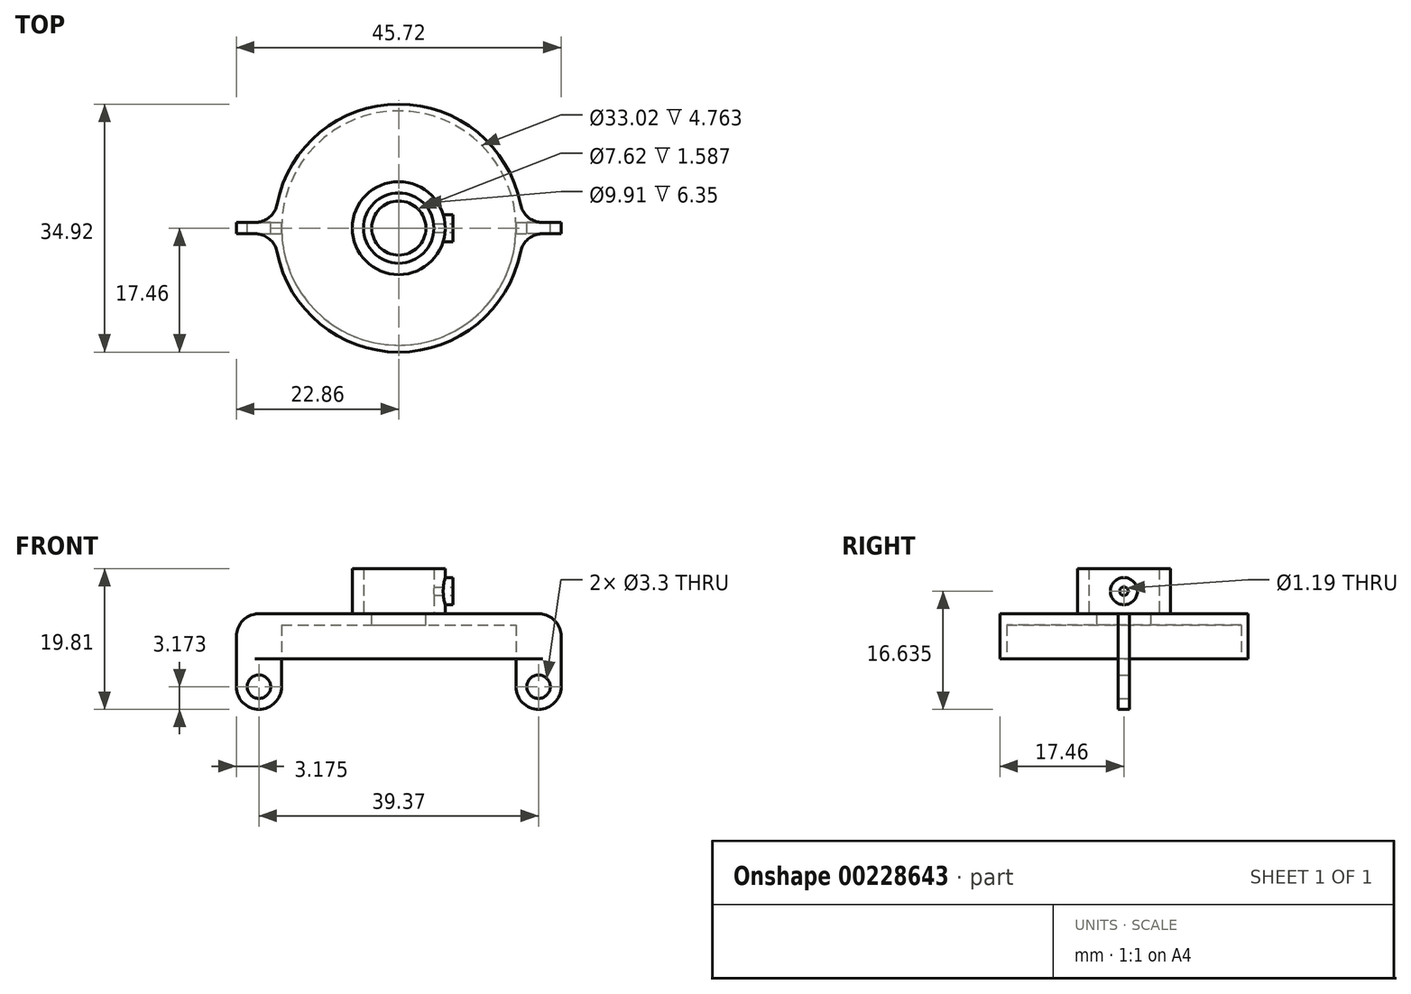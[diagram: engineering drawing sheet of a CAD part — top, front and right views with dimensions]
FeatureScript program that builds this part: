
annotation { "Feature Type Name" : "Feature", "Feature Type Description" : "" }
export const myFeature = defineFeature(function(context is Context, id is Id, definition is map)
    precondition{}
    {
        {
            var Q0;
            Q0=qCreatedBy(makeId("Top.planeOp"),FACE);
            var sketch = newSketch(context, id + "F0", { "sketchPlane" : qUnion([Q0])});
            skCircle(sketch, "E0", {"center": v(0, 0) * mm, "radius": 17.46 * mm});
            skSolve(sketch);
        }
        {
            var Q0;
            Q0 = qSketchRegion(id + "F0", true);
            extrude(context, id + "F1", {"entities" : qUnion([Q0]), "depth" : 6.35 * mm});
        }
        {
            var Q0;
            Q0=makeQuery(id+"F1.opExtrude","CAP_FACE",FACE,{"disambiguationData":[OSD([sQuery(id+"F0.wireOp",EDGE,"E0")])],"isStart":true});
            var sketch = newSketch(context, id + "F2", { "sketchPlane" : qUnion([Q0])});
            skCircle(sketch, "E1", {"center": v(0, 0) * mm, "radius": 16.51 * mm});
            skSolve(sketch);
        }
        {
            var Q0;
            Q0 = qSketchRegion(id + "F2", true);
            extrude(context, id + "F3", {"entities" : qUnion([Q0]), "operationType" : NewBodyOperationType.REMOVE, "oppositeDirection" : true, "depth" : 4.76 * mm});
        }
        {
            var Q0;
            Q0=makeQuery(id+"F1.opExtrude","CAP_FACE",FACE,{"disambiguationData":[OSD([sQuery(id+"F0.wireOp",EDGE,"E0")])],"isStart":false});
            var sketch = newSketch(context, id + "F4", { "sketchPlane" : qUnion([Q0])});
            skCircle(sketch, "E2", {"center": v(0, 0) * mm, "radius": 3.8 * mm});
            skSolve(sketch);
        }
        {
            var Q0;
            Q0 = qSketchRegion(id + "F4", true);
            extrude(context, id + "F5", {"entities" : qUnion([Q0]), "operationType" : NewBodyOperationType.REMOVE, "endBound" : BoundingType.THROUGH_ALL, "oppositeDirection" : true, "depth" : 25.4 * mm});
        }
        {
            var Q0;
            Q0=qCreatedBy(makeId("Front.planeOp"),FACE);
            var sketch = newSketch(context, id + "F6", { "sketchPlane" : qUnion([Q0])});
            skLineSegment(sketch, "E3.bottom", {"start": v(-16.51, 6.35) * mm, "end": v(-22.86, 6.35) * mm});
            skLineSegment(sketch, "E3.top", {"start": v(-16.51, -7.11) * mm, "end": v(-22.86, -7.11) * mm});
            skLineSegment(sketch, "E3.left", {"start": v(-16.51, 6.35) * mm, "end": v(-16.51, -7.11) * mm});
            skLineSegment(sketch, "E3.right", {"start": v(-22.86, 6.35) * mm, "end": v(-22.86, -7.11) * mm});
            skSolve(sketch);
        }
        {
            var Q0;
            Q0 = qSketchRegion(id + "F6", true);
            extrude(context, id + "F7", {"entities" : qUnion([Q0]), "endBound" : BoundingType.SYMMETRIC, "depth" : 1.59 * mm});
        }
        {
            var Q0;
            Q0=makeQuery(id+"F7.opExtrude","SWEPT_BODY",BODY,{"disambiguationData":[OSD([sQuery(id+"F6.wireOp",EDGE,"E3.bottom"),sQuery(id+"F6.wireOp",EDGE,"E3.top"),sQuery(id+"F6.wireOp",EDGE,"E3.left"),sQuery(id+"F6.wireOp",EDGE,"E3.right")])]});
            var Q1;
            Q1=qCreatedBy(makeId("Right.planeOp"),FACE);
            mirror(context, id + "F8", {"operationType" : NewBodyOperationType.ADD, "entities" : qUnion([Q0]), "mirrorPlane" : qUnion([Q1])});
        }
        {
            var Q0;
            Q0=makeQuery(id+"F7.opExtrude","SWEPT_EDGE",EDGE,{"disambiguationData":[OSD([sQuery(id+"F6.wireOp",EDGE,"E3.bottom"),sQuery(id+"F6.wireOp",EDGE,"E3.right")])]});
            var Q1;
            Q1=makeQuery(id+"F7.opExtrude","SWEPT_EDGE",EDGE,{"disambiguationData":[OSD([sQuery(id+"F6.wireOp",EDGE,"E3.top"),sQuery(id+"F6.wireOp",EDGE,"E3.right")])]});
            var Q2;
            Q2=makeQuery(id+"F7.opExtrude","SWEPT_EDGE",EDGE,{"disambiguationData":[OSD([sQuery(id+"F6.wireOp",EDGE,"E3.top"),sQuery(id+"F6.wireOp",EDGE,"E3.left")])]});
            var Q3;
            Q3=makeQuery(id+"F8.opPattern","COPY",EDGE,{"derivedFrom":makeQuery(id+"F7.opExtrude","SWEPT_EDGE",EDGE,{"disambiguationData":[OSD([sQuery(id+"F6.wireOp",EDGE,"E3.bottom"),sQuery(id+"F6.wireOp",EDGE,"E3.right")])]}),"instanceName":"1"});
            var Q4;
            Q4=makeQuery(id+"F8.opPattern","COPY",EDGE,{"derivedFrom":makeQuery(id+"F7.opExtrude","SWEPT_EDGE",EDGE,{"disambiguationData":[OSD([sQuery(id+"F6.wireOp",EDGE,"E3.top"),sQuery(id+"F6.wireOp",EDGE,"E3.right")])]}),"instanceName":"1"});
            var Q5;
            Q5=makeQuery(id+"F8.opPattern","COPY",EDGE,{"derivedFrom":makeQuery(id+"F7.opExtrude","SWEPT_EDGE",EDGE,{"disambiguationData":[OSD([sQuery(id+"F6.wireOp",EDGE,"E3.top"),sQuery(id+"F6.wireOp",EDGE,"E3.left")])]}),"instanceName":"1"});
            fillet(context, id + "F9", {"entities" : qUnion([Q0, Q1, Q2, Q3, Q4, Q5]), "radius" : 3.17 * mm, "tangentPropagation" : true, "allowEdgeOverflow" : false});
        }
        {
            var Q0;
            Q0=makeQuery(id+"F8.boolean.opBoolean","INTERSECT",EDGE,{"derivedFrom":[makeQuery(id+"F1.opExtrude","SWEPT_FACE",FACE,{"disambiguationData":[OSD([sQuery(id+"F0.wireOp",EDGE,"E0")])]}),makeQuery(id+"F7.opExtrude","CAP_FACE",FACE,{"disambiguationData":[OSD([sQuery(id+"F6.wireOp",EDGE,"E3.bottom"),sQuery(id+"F6.wireOp",EDGE,"E3.top"),sQuery(id+"F6.wireOp",EDGE,"E3.left"),sQuery(id+"F6.wireOp",EDGE,"E3.right")])],"isStart":false})]});
            var Q1;
            Q1=makeQuery(id+"F8.boolean.opBoolean","INTERSECT",EDGE,{"derivedFrom":[makeQuery(id+"F1.opExtrude","SWEPT_FACE",FACE,{"disambiguationData":[OSD([sQuery(id+"F0.wireOp",EDGE,"E0")])]}),makeQuery(id+"F7.opExtrude","CAP_FACE",FACE,{"disambiguationData":[OSD([sQuery(id+"F6.wireOp",EDGE,"E3.bottom"),sQuery(id+"F6.wireOp",EDGE,"E3.top"),sQuery(id+"F6.wireOp",EDGE,"E3.left"),sQuery(id+"F6.wireOp",EDGE,"E3.right")])],"isStart":true})]});
            var Q2;
            Q2=makeQuery(id+"F8.boolean.opBoolean","INTERSECT",EDGE,{"derivedFrom":[makeQuery(id+"F1.opExtrude","SWEPT_FACE",FACE,{"disambiguationData":[OSD([sQuery(id+"F0.wireOp",EDGE,"E0")])]}),makeQuery(id+"F8.opPattern","COPY",FACE,{"derivedFrom":makeQuery(id+"F7.opExtrude","CAP_FACE",FACE,{"disambiguationData":[OSD([sQuery(id+"F6.wireOp",EDGE,"E3.bottom"),sQuery(id+"F6.wireOp",EDGE,"E3.top"),sQuery(id+"F6.wireOp",EDGE,"E3.left"),sQuery(id+"F6.wireOp",EDGE,"E3.right")])],"isStart":false}),"instanceName":"1"})]});
            var Q3;
            Q3=makeQuery(id+"F8.boolean.opBoolean","INTERSECT",EDGE,{"derivedFrom":[makeQuery(id+"F1.opExtrude","SWEPT_FACE",FACE,{"disambiguationData":[OSD([sQuery(id+"F0.wireOp",EDGE,"E0")])]}),makeQuery(id+"F8.opPattern","COPY",FACE,{"derivedFrom":makeQuery(id+"F7.opExtrude","CAP_FACE",FACE,{"disambiguationData":[OSD([sQuery(id+"F6.wireOp",EDGE,"E3.bottom"),sQuery(id+"F6.wireOp",EDGE,"E3.top"),sQuery(id+"F6.wireOp",EDGE,"E3.left"),sQuery(id+"F6.wireOp",EDGE,"E3.right")])],"isStart":true}),"instanceName":"1"})]});
            fillet(context, id + "F10", {"entities" : qUnion([Q0, Q1, Q2, Q3]), "radius" : 3.17 * mm, "tangentPropagation" : true, "allowEdgeOverflow" : false});
        }
        {
            var Q0;
            Q0=makeQuery(id+"F7.opExtrude","CAP_FACE",FACE,{"disambiguationData":[OSD([sQuery(id+"F6.wireOp",EDGE,"E3.bottom"),sQuery(id+"F6.wireOp",EDGE,"E3.top"),sQuery(id+"F6.wireOp",EDGE,"E3.left"),sQuery(id+"F6.wireOp",EDGE,"E3.right")])],"isStart":true});
            var sketch = newSketch(context, id + "F11", { "sketchPlane" : qUnion([Q0])});
            skCircle(sketch, "E4", {"center": v(19.69, -3.94) * mm, "radius": 1.65 * mm});
            skCircle(sketch, "E5", {"center": v(-19.69, -3.94) * mm, "radius": 1.65 * mm});
            skSolve(sketch);
        }
        {
            var Q0;
            Q0 = qSketchRegion(id + "F11", true);
            extrude(context, id + "F12", {"entities" : qUnion([Q0]), "operationType" : NewBodyOperationType.REMOVE, "endBound" : BoundingType.THROUGH_ALL, "oppositeDirection" : true, "depth" : 25.4 * mm});
        }
        {
            var Q0;
            {var subQ0=makeQuery(id+"F7.opExtrude","SWEPT_FACE",FACE,{"disambiguationData":[OSD([sQuery(id+"F6.wireOp",EDGE,"E3.bottom")])]});Q0=makeQuery(id+"F8.boolean.opBoolean","MERGE",FACE,{"derivedFrom":[makeQuery(id+"F1.opExtrude","CAP_FACE",FACE,{"disambiguationData":[OSD([sQuery(id+"F0.wireOp",EDGE,"E0")])],"isStart":false}),subQ0,makeQuery(id+"F8.opPattern","COPY",FACE,{"derivedFrom":subQ0,"instanceName":"1"})]});}
            var sketch = newSketch(context, id + "F13", { "sketchPlane" : qUnion([Q0])});
            skCircle(sketch, "E6", {"center": v(0, 0) * mm, "radius": 4.95 * mm});
            skCircle(sketch, "E7", {"center": v(0, 0) * mm, "radius": 6.54 * mm});
            skSolve(sketch);
        }
        {
            var Q0;
            Q0 = qSketchRegion(id + "F13", true);
            extrude(context, id + "F14", {"entities" : qUnion([Q0]), "operationType" : NewBodyOperationType.ADD, "depth" : 6.35 * mm});
        }
        {
            var Q0;
            Q0=qCreatedBy(makeId("Right.planeOp"),FACE);
            cPlane(context, id + "F15", {"entities" : qUnion([Q0]), "cplaneType" : CPlaneType.OFFSET, "offset" : 7.62 * mm, "width" : 152.4 * mm, "height" : 152.4 * mm});
        }
        {
            var Q0;
            Q0=qCreatedBy(id+"F15.planeOp",FACE);
            var sketch = newSketch(context, id + "F16", { "sketchPlane" : qUnion([Q0])});
            skCircle(sketch, "E8", {"center": v(0, 9.53) * mm, "radius": 1.9 * mm});
            skSolve(sketch);
        }
        {
            var Q0;
            Q0 = qSketchRegion(id + "F16", true);
            extrude(context, id + "F17", {"entities" : qUnion([Q0]), "operationType" : NewBodyOperationType.ADD, "endBound" : BoundingType.UP_TO_NEXT, "oppositeDirection" : true, "depth" : 25.4 * mm});
        }
        {
            var Q0;
            Q0=makeQuery(id+"F17.opExtrude","CAP_FACE",FACE,{"disambiguationData":[OSD([sQuery(id+"F16.wireOp",EDGE,"E8")])],"isStart":true});
            var sketch = newSketch(context, id + "F18", { "sketchPlane" : qUnion([Q0])});
            skCircle(sketch, "E9", {"center": v(0, 9.53) * mm, "radius": 0.6 * mm});
            skSolve(sketch);
        }
        {
            var Q0;
            Q0 = qSketchRegion(id + "F18", true);
            extrude(context, id + "F19", {"entities" : qUnion([Q0]), "operationType" : NewBodyOperationType.REMOVE, "endBound" : BoundingType.UP_TO_NEXT, "oppositeDirection" : true, "depth" : 25.4 * mm});
        }
    });
